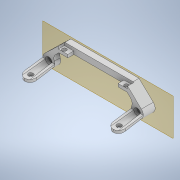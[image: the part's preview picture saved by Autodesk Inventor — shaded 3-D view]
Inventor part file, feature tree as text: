
AUTODESK INVENTOR PART (.ipt)
format: ipt  version: 2021 (Build 250183000, 183)  size: 411,136 bytes
history: native  units: mm
features: sketch x10, extrude x7, reference x4, other x4, plane x3, fillet x3, hole x1, loft x1, pattern_linear x1, projected_geometry x1
ambient origin geometry x8: Origin, YZ Plane, XZ Plane, XY Plane, X Axis, Y Axis, Z Axis, Center Point
bodies: Solid1 (feature_tree)
feature tree (35):
  extrude  "Extrusion1"  Depth=3.5mm
  plane  "Work Plane1"
  extrude  "Extrusion2"  Depth=10.0mm TaperAngle=0.0deg
  plane  "Work Plane2"
  extrude  "Extrusion3"  Depth=10.0mm TaperAngle=0.0deg
  extrude  "Extrusion4"  Depth=2.5mm TaperAngle=0.0deg
  extrude  "Extrusion5"  Depth=8.0mm
  extrude  "Extrusion6"  Depth=5.0mm
  fillet  "Fillet1"  Radius=3.5mm
  fillet  "Fillet2"  Radius=3.5mm
  hole  "Hole1"  [1 undecoded]
  plane  "Work Plane3"
  loft  "Loft1"
  pattern_linear  "Rectangular Pattern1"  Spacing1=5.0mm  [1 undecoded]
  extrude  "Extrusion8"  Depth=5.0mm
  fillet  "Fillet3"  Radius=20.0mm
  sketch  "Sketch1"  dims[d0=5.0mm d1=0.0mm d2=3.5mm]
  reference  "Reference1"
  reference  "Reference2"
  sketch  "Sketch2"  dims[d3=10.0mm d4=10.0mm d5=0.0mm]
  reference  "Reference3"
  sketch  "Sketch3"  dims[d6=57.0mm d7=10.0mm d8=0.0mm]
  reference  "Reference4"
  sketch  "Sketch4"  dims[d11=5.0mm d12=2.5mm d13=0.0mm]
  sketch  "Sketch5"  dims[d14=8.0mm d15=8.0mm]
  projected_geometry  "Projected Loop1"
  sketch  "Sketch8"  dims[d16=3.5mm d17=0.0mm d18=5.0mm d19=3.5mm d20=3.5mm]
  sketch  "Sketch10"  dims[d21=52.0mm d22=0.5mm]
  sketch  "Sketch11"  dims[d23=0.5mm d24=1.3mm]
  sketch  "Sketch12"  dims[d26=5.0mm d27=0.0mm]
  sketch  "Sketch13"  dims[d28=5.0mm d29=5.0mm d37=3.5mm d38=6.0mm d39=5.5mm d40=2.5mm d41=90.0deg d42=8.0mm d43=20.594885mm d44=5.0mm d45=20.0mm d46=0.0mm d47=90.0deg d48=0.0mm d49=90.0deg d50=20.0mm d52=74.0mm d53=4.0mm d54=4.0mm d55=5.0mm d56=5.0mm d57=5.0mm d58=5.0mm d59=0.0mm d60=0.0mm d61=5.0mm]
  parser-record x1  (decoder bookkeeping rows leaked as tree rows — omitted from the tree; the rows remain in map.json)
  other  "Assembly.iam"
  other  "Hangar:1"
  other  "LRS-50-Series(MW):1"
note: 2 required parameter values undecoded (feature->parameter linkage not recoverable at this tier; creation-order binding heuristic only, values carry confidence <= 0.55)
note: 1 file-system path scrubbed to <path> (originals preserved in map.json)
